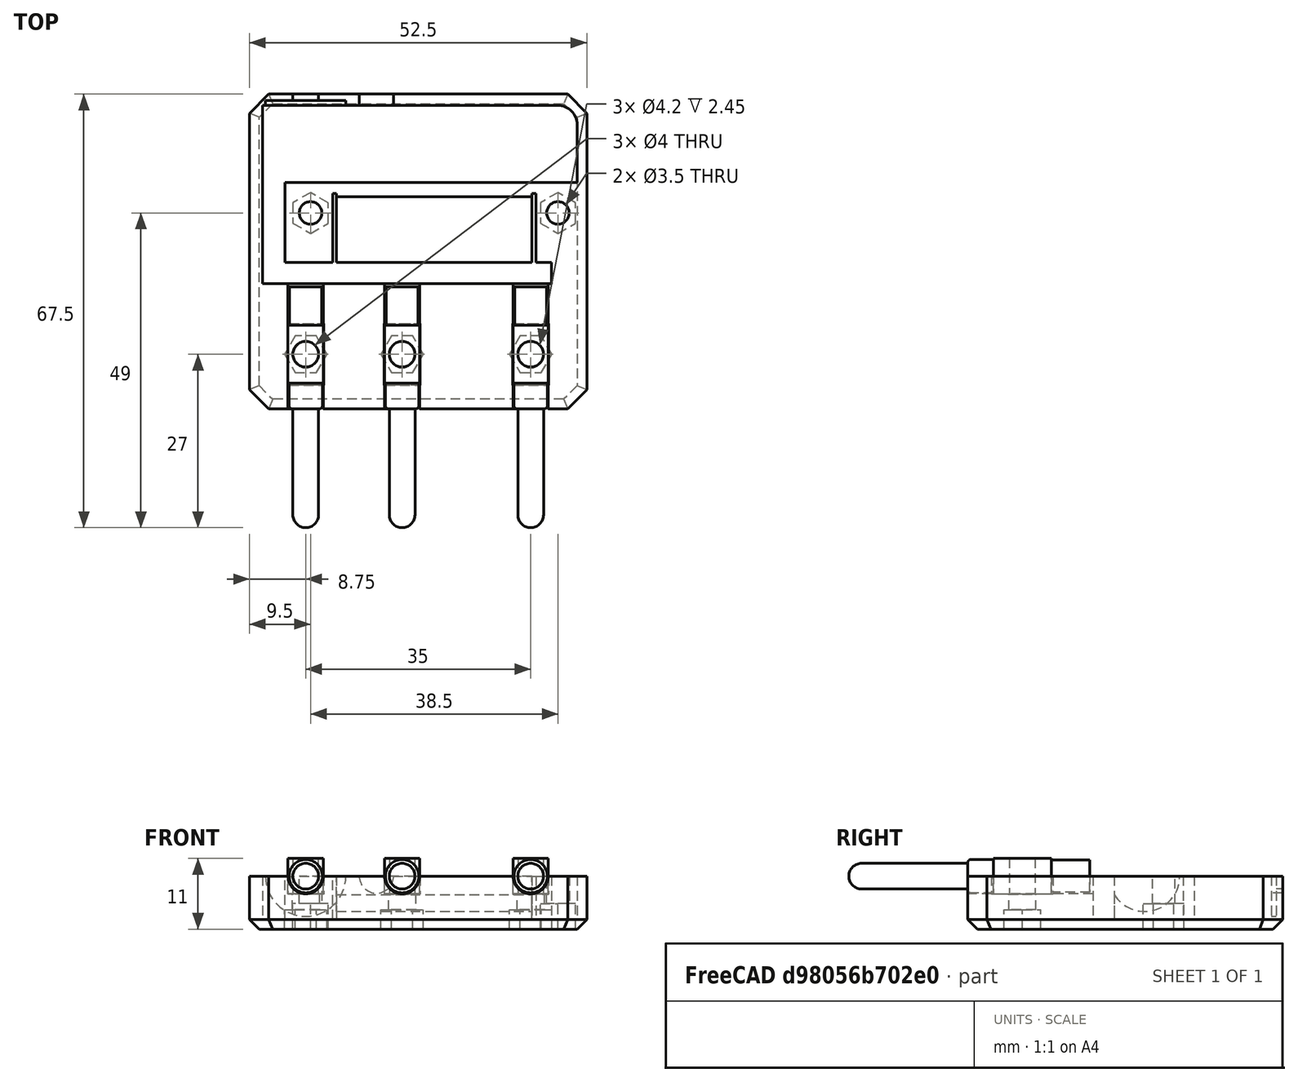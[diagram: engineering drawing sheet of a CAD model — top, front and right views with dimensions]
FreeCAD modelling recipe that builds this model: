
FCSTD DOCUMENT  (FreeCAD 0.17R10993 (Git))
Label: Zujalica
License: All rights reserved
LicenseURL: http://en.wikipedia.org/wiki/All_rights_reserved
objects: Sketcher::SketchObject×17, PartDesign::Pocket×13, PartDesign::Body×4, PartDesign::Pad×3, PartDesign::Chamfer×2, PartDesign::Revolution×1
note: 57 computed .brp shape members not serialized (recipe doc carries the construction recipe); baked Part::Feature solids carry a one-line shape summary decoded from their .brp

FEATURE [Sketcher::SketchObject] Sketch
  MapMode = 5
  Support = -> [XY_Plane]
  sketch-geometry (5):
    g0: LineSegment StartX=-2.75 StartY=4.5 StartZ=0 EndX=2.75 EndY=4.5 EndZ=0
    g1: LineSegment StartX=2.75 StartY=4.5 StartZ=0 EndX=2.75 EndY=-4.5 EndZ=0
    g2: LineSegment StartX=2.75 StartY=-4.5 StartZ=0 EndX=-2.75 EndY=-4.5 EndZ=0
    g3: LineSegment StartX=-2.75 StartY=-4.5 StartZ=0 EndX=-2.75 EndY=4.5 EndZ=0
    g4: Circle CenterX=0 CenterY=0 CenterZ=0 NormalX=0 NormalY=0 NormalZ=1 Radius=2
  constraints (14):
    c: Coincident(g0,g1)
    c: Coincident(g1,g2)
    c: Coincident(g2,g3)
    c: Coincident(g3,g0)
    c: Horizontal(g0)
    c: Horizontal(g2)
    c: Vertical(g1)
    c: Vertical(g3)
    c: Symmetric(g2,g1,g-2)
    c: Symmetric(g2,g0,g-1)
    c: DistanceX(g2,g2) = 5.5
    c: DistanceY(g1,g1) = 9
    c: Coincident(g4,g-1)
    c: Radius(g4) = 2
FEATURE [PartDesign::Pad] Pad
  Length = 5.5
  Length2 = 100
  Midplane = true
  Profile = -> Sketch
  Type = 0
FEATURE [Sketcher::SketchObject] Sketch001
  MapMode = 5
  Placement = pos=(0,4.5,0) rot=(0,0.707107,0.707107;3.14159rad)
  Support = -> [Pad]
  sketch-geometry (1):
    g0: Circle CenterX=0 CenterY=0 CenterZ=0 NormalX=0 NormalY=0 NormalZ=1 Radius=2.5
  constraints (2):
    c: Coincident(g0,g-1)
    c: Radius(g0) = 2.5
FEATURE [PartDesign::Pad] Pad001
  BaseFeature = -> Pad
  Length = 6
  Length2 = 100
  Profile = -> Sketch001
  Type = 0
FEATURE [Sketcher::SketchObject] Sketch002
  MapMode = 5
  Support = -> [XY_Plane]
  sketch-geometry (7):
    g0: LineSegment StartX=0 StartY=-4.5 StartZ=0 EndX=2.6 EndY=-4.5 EndZ=0
    g1: LineSegment StartX=2.6 StartY=-4.5 StartZ=0 EndX=2.6 EndY=-8 EndZ=0
    g2: LineSegment StartX=2.1 StartY=-8.5 StartZ=0 EndX=2 EndY=-8.5 EndZ=0
    g3: LineSegment StartX=2 StartY=-8.5 StartZ=0 EndX=2 EndY=-25 EndZ=0
    g4: ArcOfCircle CenterX=0 CenterY=-25 CenterZ=0 NormalX=0 NormalY=0 NormalZ=1 Radius=2 StartAngle=4.71239 EndAngle=6.28319
    g5: LineSegment StartX=0 StartY=-27 StartZ=0 EndX=0 EndY=-4.5 EndZ=0
    g6: ArcOfCircle CenterX=2.1 CenterY=-8 CenterZ=0 NormalX=0 NormalY=0 NormalZ=1 Radius=0.5 StartAngle=4.71239 EndAngle=6.28319
  constraints (21):
    c: PointOnObject(g0,g-2)
    c: Horizontal(g0)
    c: Coincident(g0,g1)
    c: Vertical(g1)
    c: Horizontal(g2)
    c: Coincident(g2,g3)
    c: Vertical(g3)
    c: PointOnObject(g4,g-2)
    c: Coincident(g4,g3)
    c: PointOnObject(g4,g-2)
    c: Coincident(g5,g4)
    c: Coincident(g5,g0)
    c: DistanceX(g0,g0) = 2.6
    c: Tangent(g4,g3)
    c: Radius(g4) = 2
    c: DistanceY(g5,g5) = 22.5
    c: DistanceY(g0,g-1) = 4.5
    c: Tangent(g2,g6) = 1.5708
    c: Tangent(g1,g6) = 1.5708
    c: Radius(g6) = 0.5
    c: DistanceY(g2,g0) = 4
FEATURE [PartDesign::Revolution] Revolution
  Angle = 360
  Axis = (0,1,0)
  Base = (0,0,0)
  BaseFeature = -> Pad001
  Profile = -> Sketch002
  ReferenceAxis = -> Sketch002 [V_Axis]
  Reversed = true
FEATURE [PartDesign::Body] Body  label="Banana"
  Group = -> [Sketch,Pad,Sketch001,Pad001,Sketch002,Revolution]
  Origin = -> BodyOrigin
  Tip = -> Revolution
FEATURE [PartDesign::Body] Body001  label="Banana001"
  Group = -> [Sketch,Pad,Sketch001,Pad001,Sketch002,Revolution]
  Origin = -> BodyOrigin
  Placement = pos=(15,0,0) rot=(0,0,1;0rad)
  Tip = -> Revolution
FEATURE [PartDesign::Body] Body002  label="Banana002"
  Group = -> [Sketch,Pad,Sketch001,Pad001,Sketch002,Revolution]
  Origin = -> BodyOrigin
  Placement = pos=(35,0,0) rot=(0,0,1;0rad)
  Tip = -> Revolution
FEATURE [Sketcher::SketchObject] Sketch003
  MapMode = 5
  Support = -> [XY_Plane001]
  expr: Constraints[10] = Sketch003.Constraints.udaljenost_L * 2 + 35mm
  sketch-geometry (4):
    g0: LineSegment StartX=-8.75 StartY=40.5 StartZ=0 EndX=43.75 EndY=40.5 EndZ=0
    g1: LineSegment StartX=43.75 StartY=40.5 StartZ=0 EndX=43.75 EndY=-8.5 EndZ=0
    g2: LineSegment StartX=43.75 StartY=-8.5 StartZ=0 EndX=-8.75 EndY=-8.5 EndZ=0
    g3: LineSegment StartX=-8.75 StartY=-8.5 StartZ=0 EndX=-8.75 EndY=40.5 EndZ=0
  constraints (12):
    c: Coincident(g0,g1)
    c: Coincident(g1,g2)
    c: Coincident(g2,g3)
    c: Coincident(g3,g0)
    c: Horizontal(g0)
    c: Horizontal(g2)
    c: Vertical(g1)
    c: Vertical(g3)
    c: DistanceY(g2,g-1) = 8.5
    c: DistanceX(g2,g-1) = 8.75  'udaljenost_L'
    c: DistanceX(g2,g2) = 52.5
    c: DistanceY(g1,g1) = 49
FEATURE [PartDesign::Pad] Pad002
  Length = 8.25
  Length2 = 100
  Profile = -> Sketch003
  Reversed = true
  Type = 0
FEATURE [Sketcher::SketchObject] Sketch004
  MapMode = 5
  Support = -> [XY_Plane001]
  sketch-geometry (12):
    g0: LineSegment StartX=-2.8 StartY=4.8 StartZ=0 EndX=2.8 EndY=4.8 EndZ=0
    g1: LineSegment StartX=2.8 StartY=4.8 StartZ=0 EndX=2.8 EndY=-4.8 EndZ=0
    g2: LineSegment StartX=2.8 StartY=-4.8 StartZ=0 EndX=-2.8 EndY=-4.8 EndZ=0
    g3: LineSegment StartX=-2.8 StartY=-4.8 StartZ=0 EndX=-2.8 EndY=4.8 EndZ=0
    g4: LineSegment StartX=12.2 StartY=4.8 StartZ=0 EndX=17.8 EndY=4.8 EndZ=0
    g5: LineSegment StartX=17.8 StartY=4.8 StartZ=0 EndX=17.8 EndY=-4.8 EndZ=0
    g6: LineSegment StartX=17.8 StartY=-4.8 StartZ=0 EndX=12.2 EndY=-4.8 EndZ=0
    g7: LineSegment StartX=12.2 StartY=-4.8 StartZ=0 EndX=12.2 EndY=4.8 EndZ=0
    g8: LineSegment StartX=32.2 StartY=4.8 StartZ=0 EndX=37.8 EndY=4.8 EndZ=0
    g9: LineSegment StartX=37.8 StartY=4.8 StartZ=0 EndX=37.8 EndY=-4.8 EndZ=0
    g10: LineSegment StartX=37.8 StartY=-4.8 StartZ=0 EndX=32.2 EndY=-4.8 EndZ=0
    g11: LineSegment StartX=32.2 StartY=-4.8 StartZ=0 EndX=32.2 EndY=4.8 EndZ=0
  constraints (36):
    c: Coincident(g0,g1)
    c: Coincident(g1,g2)
    c: Coincident(g2,g3)
    c: Coincident(g3,g0)
    c: Horizontal(g0)
    c: Horizontal(g2)
    c: Vertical(g1)
    c: Vertical(g3)
    c: Symmetric(g0,g0,g-2)
    c: Symmetric(g2,g0,g-1)
    c: DistanceY(g3,g3) = 9.6
    c: DistanceX(g2,g2) = 5.6
    c: Coincident(g4,g5)
    c: Coincident(g5,g6)
    c: Coincident(g6,g7)
    c: Coincident(g7,g4)
    c: Horizontal(g4)
    c: Horizontal(g6)
    c: Vertical(g5)
    c: Vertical(g7)
    c: Coincident(g8,g9)
    c: Coincident(g9,g10)
    c: Coincident(g10,g11)
    c: Coincident(g11,g8)
    c: Horizontal(g8)
    c: Horizontal(g10)
    c: Vertical(g9)
    c: Vertical(g11)
    c: Equal(g8,g4)
    c: Equal(g4,g0)
    c: Equal(g1,g5)
    c: Equal(g5,g9)
    c: Symmetric(g4,g6,g-1)
    c: Symmetric(g8,g10,g-1)
    c: DistanceX(g2,g6) = 15
    c: DistanceX(g2,g10) = 35
FEATURE [PartDesign::Pocket] Pocket
  BaseFeature = -> Pad002
  Length = 2.8
  Profile = -> Sketch004
  Type = 0
FEATURE [Sketcher::SketchObject] Sketch005
  MapMode = 5
  Placement = pos=(0,0,0) rot=(1,0,0;1.5708rad)
  Support = -> [XZ_Plane001]
  sketch-geometry (3):
    g0: Circle CenterX=0 CenterY=0 CenterZ=0 NormalX=0 NormalY=0 NormalZ=1 Radius=2.75
    g1: Circle CenterX=15 CenterY=0 CenterZ=0 NormalX=0 NormalY=0 NormalZ=1 Radius=2.75
    g2: Circle CenterX=35 CenterY=0 CenterZ=0 NormalX=0 NormalY=0 NormalZ=1 Radius=2.75
  constraints (8):
    c: Coincident(g0,g-1)
    c: PointOnObject(g1,g-1)
    c: PointOnObject(g2,g-1)
    c: DistanceX(g-1,g1) = 15
    c: DistanceX(g1,g2) = 20
    c: Radius(g0) = 2.75
    c: Equal(g0,g1)
    c: Equal(g0,g2)
FEATURE [PartDesign::Pocket] Pocket001
  BaseFeature = -> Pocket
  Length = 22
  Midplane = true
  Profile = -> Sketch005
  Type = 0
FEATURE [Sketcher::SketchObject] Sketch006
  MapMode = 5
  Support = -> [XY_Plane001]
  sketch-geometry (3):
    g0: Circle CenterX=0 CenterY=0 CenterZ=0 NormalX=0 NormalY=0 NormalZ=1 Radius=2.1
    g1: Circle CenterX=15 CenterY=0 CenterZ=0 NormalX=0 NormalY=0 NormalZ=1 Radius=2.1
    g2: Circle CenterX=35 CenterY=0 CenterZ=0 NormalX=0 NormalY=0 NormalZ=1 Radius=2.1
  constraints (8):
    c: Coincident(g0,g-1)
    c: PointOnObject(g1,g-1)
    c: PointOnObject(g2,g-1)
    c: DistanceX(g-1,g1) = 15
    c: DistanceX(g1,g2) = 20
    c: Radius(g0) = 2.1
    c: Equal(g0,g1)
    c: Equal(g0,g2)
FEATURE [PartDesign::Pocket] Pocket002
  BaseFeature = -> Pocket001
  Length = 5
  Profile = -> Sketch006
  Type = 1
FEATURE [Sketcher::SketchObject] Sketch007
  MapMode = 5
  Placement = pos=(0,0,-8.25) rot=(0,0,1;0rad)
  Support = -> [XY_Plane001]
  superPlacement = pos=(0,0,-8.25) rot=(0,0,1;0rad)
  sketch-geometry (21):
    g0: LineSegment StartX=1.64545 StartY=2.85 StartZ=0 EndX=-1.64545 EndY=2.85 EndZ=0
    g1: LineSegment StartX=-1.64545 StartY=2.85 StartZ=0 EndX=-3.2909 EndY=0 EndZ=0
    g2: LineSegment StartX=-3.2909 StartY=0 StartZ=0 EndX=-1.64545 EndY=-2.85 EndZ=0
    g3: LineSegment StartX=-1.64545 StartY=-2.85 StartZ=0 EndX=1.64545 EndY=-2.85 EndZ=0
    g4: LineSegment StartX=1.64545 StartY=-2.85 StartZ=0 EndX=3.2909 EndY=0 EndZ=0
    g5: LineSegment StartX=3.2909 StartY=0 StartZ=0 EndX=1.64545 EndY=2.85 EndZ=0
    g6: Circle [constr] CenterX=0 CenterY=0 CenterZ=0 NormalX=0 NormalY=0 NormalZ=1 Radius=3.2909
    g7: LineSegment StartX=16.6454 StartY=-2.85 StartZ=0 EndX=18.2909 EndY=0 EndZ=0
    g8: LineSegment StartX=18.2909 StartY=0 StartZ=0 EndX=16.6454 EndY=2.85 EndZ=0
    g9: LineSegment StartX=16.6454 StartY=2.85 StartZ=0 EndX=13.3546 EndY=2.85 EndZ=0
    g10: LineSegment StartX=13.3546 StartY=2.85 StartZ=0 EndX=11.7091 EndY=0 EndZ=0
    g11: LineSegment StartX=11.7091 StartY=0 StartZ=0 EndX=13.3546 EndY=-2.85 EndZ=0
    g12: LineSegment StartX=13.3546 StartY=-2.85 StartZ=0 EndX=16.6454 EndY=-2.85 EndZ=0
    g13: Circle [constr] CenterX=15 CenterY=0 CenterZ=0 NormalX=0 NormalY=0 NormalZ=1 Radius=3.2909
    g14: LineSegment StartX=36.6454 StartY=-2.85 StartZ=0 EndX=38.2909 EndY=0 EndZ=0
    g15: LineSegment StartX=38.2909 StartY=0 StartZ=0 EndX=36.6454 EndY=2.85 EndZ=0
    g16: LineSegment StartX=36.6454 StartY=2.85 StartZ=0 EndX=33.3546 EndY=2.85 EndZ=0
    g17: LineSegment StartX=33.3546 StartY=2.85 StartZ=0 EndX=31.7091 EndY=0 EndZ=0
    g18: LineSegment StartX=31.7091 StartY=0 StartZ=0 EndX=33.3546 EndY=-2.85 EndZ=0
    g19: LineSegment StartX=33.3546 StartY=-2.85 StartZ=0 EndX=36.6454 EndY=-2.85 EndZ=0
    g20: Circle [constr] CenterX=35 CenterY=0 CenterZ=0 NormalX=0 NormalY=0 NormalZ=1 Radius=3.2909
  constraints (50):
    c: Coincident(g0,g1)
    c: Coincident(g1,g2)
    c: Coincident(g2,g3)
    c: Coincident(g3,g4)
    c: Coincident(g4,g5)
    c: Coincident(g5,g0)
    c: Equal(g0, g1-g5) x5
    c: PointOnObject(g0,g6)
    c: PointOnObject(g1,g6)
    c: PointOnObject(g2,g6)
    c: PointOnObject(g3,g6)
    c: PointOnObject(g4,g6)
    c: PointOnObject(g5,g6)
    c: Coincident(g6,g-1)
    c: Horizontal(g3)
    c: DistanceY(g2,g0) = 5.7
    c: Coincident(g7,g8)
    c: Coincident(g8,g9)
    c: Coincident(g9,g10)
    c: Coincident(g10,g11)
    c: Coincident(g11,g12)
    c: Coincident(g12,g7)
    c: Equal(g7, g8-g12) x5
    c: PointOnObject(g7,g13)
    c: PointOnObject(g8,g13)
    c: PointOnObject(g9,g13)
    c: PointOnObject(g10,g13)
    c: PointOnObject(g11,g13)
    c: PointOnObject(g12,g13)
    c: PointOnObject(g13,g-1)
    c: Coincident(g14,g15)
    c: Coincident(g15,g16)
    c: Coincident(g16,g17)
    c: Coincident(g17,g18)
    c: Coincident(g18,g19)
    c: Coincident(g19,g14)
    c: Equal(g14, g15-g19) x5
    c: PointOnObject(g14,g20)
    c: PointOnObject(g15,g20)
    c: PointOnObject(g16,g20)
    c: PointOnObject(g17,g20)
    c: PointOnObject(g18,g20)
    c: PointOnObject(g19,g20)
    c: PointOnObject(g20,g-1)
    c: Horizontal(g12)
    c: Horizontal(g19)
    c: DistanceX(g-1,g13) = 15
    c: DistanceX(g13,g20) = 20
    c: Equal(g3,g12)
    c: Equal(g12,g19)
FEATURE [PartDesign::Pocket] Pocket003
  BaseFeature = -> Pocket002
  Length = 3
  Profile = -> Sketch007
  Reversed = true
  Type = 0
FEATURE [Sketcher::SketchObject] Sketch008
  MapMode = 5
  Placement = pos=(20,19,0) rot=(0.57735,0.57735,0.57735;2.0944rad)
  Support = -> [YZ_Plane001]
  superPlacement = pos=(19,0,20) rot=(0,0,1;0rad)
  sketch-geometry (1):
    g0: Circle CenterX=0 CenterY=0 CenterZ=0 NormalX=0 NormalY=0 NormalZ=1 Radius=5.5
  constraints (2):
    c: Coincident(g0,g-1)
    c: Radius(g0) = 5.5
FEATURE [PartDesign::Pocket] Pocket004
  BaseFeature = -> Pocket003
  Length = 31
  Midplane = true
  Profile = -> Sketch008
  Type = 0
FEATURE [Sketcher::SketchObject] Sketch009
  MapMode = 5
  Support = -> [XY_Plane001]
  expr: Constraints[8] = Sketch003.Constraints[8]
  expr: Constraints.udaljenost_L = Sketch003.Constraints[9]
  expr: Constraints[10] = Sketch003.Constraints[10]
  expr: Constraints[11] = Sketch003.Constraints[11]
  sketch-geometry (9):
    g0: LineSegment [constr] StartX=-8.75 StartY=40.5 StartZ=0 EndX=43.75 EndY=40.5 EndZ=0
    g1: LineSegment [constr] StartX=43.75 StartY=40.5 StartZ=0 EndX=43.75 EndY=-8.5 EndZ=0
    g2: LineSegment [constr] StartX=43.75 StartY=-8.5 StartZ=0 EndX=-8.75 EndY=-8.5 EndZ=0
    g3: LineSegment [constr] StartX=-8.75 StartY=-8.5 StartZ=0 EndX=-8.75 EndY=40.5 EndZ=0
    g4: LineSegment StartX=-6.75 StartY=38.75 StartZ=0 EndX=39.25 EndY=38.75 EndZ=0
    g5: LineSegment StartX=42.25 StartY=35.75 StartZ=0 EndX=42.25 EndY=26.75 EndZ=0
    g6: LineSegment StartX=42.25 StartY=26.75 StartZ=0 EndX=-6.75 EndY=26.75 EndZ=0
    g7: LineSegment StartX=-6.75 StartY=26.75 StartZ=0 EndX=-6.75 EndY=38.75 EndZ=0
    g8: ArcOfCircle CenterX=39.25 CenterY=35.75 CenterZ=0 NormalX=0 NormalY=0 NormalZ=1 Radius=3 StartAngle=0 EndAngle=1.5708
  constraints (26):
    c: Coincident(g0,g1)
    c: Coincident(g1,g2)
    c: Coincident(g2,g3)
    c: Coincident(g3,g0)
    c: Horizontal(g0)
    c: Horizontal(g2)
    c: Vertical(g1)
    c: Vertical(g3)
    c: DistanceY(g2,g-1) = 8.5
    c: DistanceX(g2,g-1) = 8.75  'udaljenost_L'
    c: DistanceX(g2,g2) = 52.5
    c: DistanceY(g1,g1) = 49
    c: Coincident(g6,g7)
    c: Coincident(g7,g4)
    c: Horizontal(g4)
    c: Horizontal(g6)
    c: Vertical(g5)
    c: Vertical(g7)
    c: DistanceY(g7,g7) = 12
    c: DistanceX(g0,g4) = 2
    c: Tangent(g4,g8) = 1.5708
    c: Tangent(g5,g8) = 1.5708
    c: Radius(g8) = 3
    c: DistanceX(g5,g0) = 1.5
    c: DistanceY(g4,g0) = 1.75
    c: Coincident(g5,g6)
FEATURE [PartDesign::Pocket] Pocket005
  BaseFeature = -> Pocket004
  Length = 6.75
  Profile = -> Sketch009
  Type = 0
FEATURE [Sketcher::SketchObject] Sketch010
  MapMode = 5
  Placement = pos=(0,39.5,0) rot=(1,0,0;1.5708rad)
  Support = -> [XZ_Plane001]
  superPlacement = pos=(0,0,-39.5) rot=(0,0,1;0rad)
  sketch-geometry (1):
    g0: Circle CenterX=0 CenterY=0 CenterZ=0 NormalX=0 NormalY=0 NormalZ=1 Radius=6.25
  constraints (2):
    c: Coincident(g0,g-1)
    c: Radius(g0) = 6.25
FEATURE [PartDesign::Pocket] Pocket006
  BaseFeature = -> Pocket005
  Length = 12
  Profile = -> Sketch010
  Reversed = true
  Type = 0
FEATURE [Sketcher::SketchObject] Sketch011
  MapMode = 5
  Support = -> [XY_Plane001]
  sketch-geometry (6):
    g0: LineSegment StartX=-6.75 StartY=27 StartZ=0 EndX=-3.25 EndY=27 EndZ=0
    g1: LineSegment StartX=-3.25 StartY=27 StartZ=0 EndX=-3.25 EndY=14.3 EndZ=0
    g2: LineSegment StartX=38.25 StartY=11 StartZ=0 EndX=-6.75 EndY=11 EndZ=0
    g3: LineSegment StartX=-6.75 StartY=11 StartZ=0 EndX=-6.75 EndY=27 EndZ=0
    g4: LineSegment StartX=-3.25 StartY=14.3 StartZ=0 EndX=38.25 EndY=14.3 EndZ=0
    g5: LineSegment StartX=38.25 StartY=14.3 StartZ=0 EndX=38.25 EndY=11 EndZ=0
  constraints (18):
    c: Coincident(g0,g1)
    c: Coincident(g2,g3)
    c: Coincident(g3,g0)
    c: Horizontal(g0)
    c: Horizontal(g2)
    c: Vertical(g1)
    c: Vertical(g3)
    c: DistanceY(g-1,g2) = 11
    c: DistanceX(g2,g-1) = 6.75
    c: DistanceY(g3,g3) = 16
    c: DistanceX(g0,g0) = 3.5
    c: Horizontal(g4)
    c: Coincident(g4,g5)
    c: Coincident(g1,g4)
    c: Coincident(g2,g5)
    c: Vertical(g5)
    c: DistanceY(g5,g5) = 3.3
    c: DistanceX(g2,g2) = 45
FEATURE [Sketcher::SketchObject] Sketch012
  MapMode = 5
  Placement = pos=(11,39.5,0) rot=(1,0,0;1.5708rad)
  Support = -> [XZ_Plane001]
  superPlacement = pos=(11,0,-39.5) rot=(0,0,1;0rad)
  expr: superPlacement.Base.x = 2.5 + 12 / 2 + 5 / 2
  sketch-geometry (1):
    g0: Circle CenterX=0 CenterY=0 CenterZ=0 NormalX=0 NormalY=0 NormalZ=1 Radius=2.65
  constraints (2):
    c: Coincident(g0,g-1)
    c: Radius(g0) = 2.65
FEATURE [PartDesign::Pocket] Pocket008
  BaseFeature = -> Pocket006
  Length = 5
  Midplane = true
  Profile = -> Sketch012
  Type = 0
FEATURE [Sketcher::SketchObject] Sketch013
  MapMode = 5
  Placement = pos=(0,39.5,0) rot=(1,0,0;1.5708rad)
  Support = -> [XZ_Plane001]
  superPlacement = pos=(0,0,-39.5) rot=(0,0,1;0rad)
  sketch-geometry (1):
    g0: Circle CenterX=0 CenterY=0 CenterZ=0 NormalX=0 NormalY=0 NormalZ=1 Radius=2
  constraints (2):
    c: Coincident(g0,g-1)
    c: Radius(g0) = 2
FEATURE [PartDesign::Pocket] Pocket009
  BaseFeature = -> Pocket008
  Length = 5
  Profile = -> Sketch013
  Type = 0
FEATURE [PartDesign::Pocket] Pocket007
  BaseFeature = -> Pocket009
  Length = 6.75
  Profile = -> Sketch011
  Type = 0
FEATURE [Sketcher::SketchObject] Sketch014
  MapMode = 5
  Support = -> [XY_Plane001]
  sketch-geometry (2):
    g0: Circle CenterX=0.75 CenterY=22 CenterZ=0 NormalX=0 NormalY=0 NormalZ=1 Radius=1.75
    g1: Circle CenterX=39.25 CenterY=22 CenterZ=0 NormalX=0 NormalY=0 NormalZ=1 Radius=1.75
  constraints (6):
    c: Radius(g1) = 1.75
    c: Equal(g1,g0)
    c: DistanceY(g-1,g0) = 22
    c: DistanceY(g-1,g1) = 22
    c: DistanceX(g-1,g0) = 0.75
    c: DistanceX(g0,g1) = 38.5
FEATURE [PartDesign::Pocket] Pocket010
  BaseFeature = -> Pocket007
  Length = 5
  Profile = -> Sketch014
  Type = 1
FEATURE [Sketcher::SketchObject] Sketch015
  MapMode = 5
  Placement = pos=(0,0,-8.25) rot=(0,0,1;0rad)
  Support = -> [XY_Plane001]
  superPlacement = pos=(0,0,-8.25) rot=(0,0,1;0rad)
  sketch-geometry (16):
    g0: Circle [constr] CenterX=0.75 CenterY=22 CenterZ=0 NormalX=0 NormalY=0 NormalZ=1 Radius=1.75
    g1: Circle [constr] CenterX=39.25 CenterY=22 CenterZ=0 NormalX=0 NormalY=0 NormalZ=1 Radius=1.75
    g2: LineSegment StartX=3.5 StartY=20.4123 StartZ=0 EndX=3.5 EndY=23.5877 EndZ=0
    g3: LineSegment StartX=3.5 StartY=23.5877 StartZ=0 EndX=0.75 EndY=25.1754 EndZ=0
    g4: LineSegment StartX=0.75 StartY=25.1754 StartZ=0 EndX=-2 EndY=23.5877 EndZ=0
    g5: LineSegment StartX=-2 StartY=23.5877 StartZ=0 EndX=-2 EndY=20.4123 EndZ=0
    g6: LineSegment StartX=-2 StartY=20.4123 StartZ=0 EndX=0.75 EndY=18.8246 EndZ=0
    g7: LineSegment StartX=0.75 StartY=18.8246 StartZ=0 EndX=3.5 EndY=20.4123 EndZ=0
    g8: Circle [constr] CenterX=0.75 CenterY=22 CenterZ=0 NormalX=0 NormalY=0 NormalZ=1 Radius=3.17543
    g9: LineSegment StartX=42 StartY=20.4123 StartZ=0 EndX=42 EndY=23.5877 EndZ=0
    g10: LineSegment StartX=42 StartY=23.5877 StartZ=0 EndX=39.25 EndY=25.1754 EndZ=0
    g11: LineSegment StartX=39.25 StartY=25.1754 StartZ=0 EndX=36.5 EndY=23.5877 EndZ=0
    g12: LineSegment StartX=36.5 StartY=23.5877 StartZ=0 EndX=36.5 EndY=20.4123 EndZ=0
    g13: LineSegment StartX=36.5 StartY=20.4123 StartZ=0 EndX=39.25 EndY=18.8246 EndZ=0
    g14: LineSegment StartX=39.25 StartY=18.8246 StartZ=0 EndX=42 EndY=20.4123 EndZ=0
    g15: Circle [constr] CenterX=39.25 CenterY=22 CenterZ=0 NormalX=0 NormalY=0 NormalZ=1 Radius=3.17543
  constraints (38):
    c: Radius(g1) = 1.75
    c: Equal(g1,g0)
    c: DistanceY(g-1,g0) = 22
    c: DistanceY(g-1,g1) = 22
    c: DistanceX(g-1,g0) = 0.75
    c: DistanceX(g0,g1) = 38.5
    c: Coincident(g2,g3)
    c: Coincident(g3,g4)
    c: Coincident(g4,g5)
    c: Coincident(g5,g6)
    c: Coincident(g6,g7)
    c: Coincident(g7,g2)
    c: Equal(g2, g3-g7) x5
    c: PointOnObject(g2,g8)
    c: PointOnObject(g3,g8)
    c: PointOnObject(g4,g8)
    c: PointOnObject(g5,g8)
    c: PointOnObject(g6,g8)
    c: PointOnObject(g7,g8)
    c: Coincident(g8,g0)
    c: Coincident(g9,g10)
    c: Coincident(g10,g11)
    c: Coincident(g11,g12)
    c: Coincident(g12,g13)
    c: Coincident(g13,g14)
    c: Coincident(g14,g9)
    c: Equal(g9, g10-g14) x5
    c: PointOnObject(g9,g15)
    c: PointOnObject(g10,g15)
    c: PointOnObject(g11,g15)
    c: PointOnObject(g12,g15)
    c: PointOnObject(g13,g15)
    c: PointOnObject(g14,g15)
    c: Coincident(g15,g1)
    c: Vertical(g2)
    c: Vertical(g12)
    c: Equal(g2,g12)
    c: DistanceX(g4,g2) = 5.5
FEATURE [PartDesign::Pocket] Pocket011
  BaseFeature = -> Pocket010
  Length = 4
  Profile = -> Sketch015
  Reversed = true
  Type = 0
FEATURE [PartDesign::Chamfer] Chamfer
  Base = -> Pocket011 [Edge6,Edge71,Edge37,Edge4]
  BaseFeature = -> Pocket011
  Size = 3
FEATURE [PartDesign::Chamfer] Chamfer001
  Base = -> Chamfer [Edge42,Edge41,Edge39,Edge34,Edge4,Edge37,Edge38,Edge40]
  BaseFeature = -> Chamfer
  Size = 1.5
FEATURE [Sketcher::SketchObject] Sketch016
  MapMode = 5
  Support = -> [XY_Plane001]
  sketch-geometry (8):
    g0: LineSegment StartX=4.2 StartY=25 StartZ=0 EndX=4.8 EndY=25 EndZ=0
    g1: LineSegment StartX=4.8 StartY=25 StartZ=0 EndX=4.8 EndY=13 EndZ=0
    g2: LineSegment StartX=4.8 StartY=13 StartZ=0 EndX=4.2 EndY=13 EndZ=0
    g3: LineSegment StartX=4.2 StartY=13 StartZ=0 EndX=4.2 EndY=25 EndZ=0
    g4: LineSegment StartX=35.2 StartY=25 StartZ=0 EndX=35.8 EndY=25 EndZ=0
    g5: LineSegment StartX=35.8 StartY=25 StartZ=0 EndX=35.8 EndY=13 EndZ=0
    g6: LineSegment StartX=35.8 StartY=13 StartZ=0 EndX=35.2 EndY=13 EndZ=0
    g7: LineSegment StartX=35.2 StartY=13 StartZ=0 EndX=35.2 EndY=25 EndZ=0
  constraints (24):
    c: Coincident(g0,g1)
    c: Coincident(g1,g2)
    c: Coincident(g2,g3)
    c: Coincident(g3,g0)
    c: Horizontal(g0)
    c: Horizontal(g2)
    c: Vertical(g1)
    c: Vertical(g3)
    c: Coincident(g4,g5)
    c: Coincident(g5,g6)
    c: Coincident(g6,g7)
    c: Coincident(g7,g4)
    c: Horizontal(g4)
    c: Horizontal(g6)
    c: Vertical(g5)
    c: Vertical(g7)
    c: Equal(g0,g4)
    c: DistanceX(g0,g0) = 0.6
    c: Horizontal(g0,g4)
    c: Equal(g3,g5)
    c: DistanceY(g5,g5) = 12
    c: DistanceX(g0,g4) = 30.4
    c: DistanceX(g-1,g2) = 4.2
    c: DistanceY(g-1,g0) = 25
FEATURE [PartDesign::Pocket] Pocket012
  BaseFeature = -> Chamfer001
  Length = 6.75
  Profile = -> Sketch016
  Type = 0
FEATURE [PartDesign::Body] Body003
  Group = -> [Sketch003,Pad002,Sketch004,Pocket,Sketch005,Pocket001,Sketch006,Pocket002,Sketch007,Pocket003,Sketch008,Pocket004,Sketch009,Pocket005,Sketch010,Pocket006,Sketch011,Sketch012,Pocket008,Sketch013,Pocket009,Pocket007,Sketch014,Pocket010,Sketch015,Pocket011,Chamfer,Chamfer001,Sketch016,Pocket012]
  Origin = -> Body003Origin
  Tip = -> Pocket012
